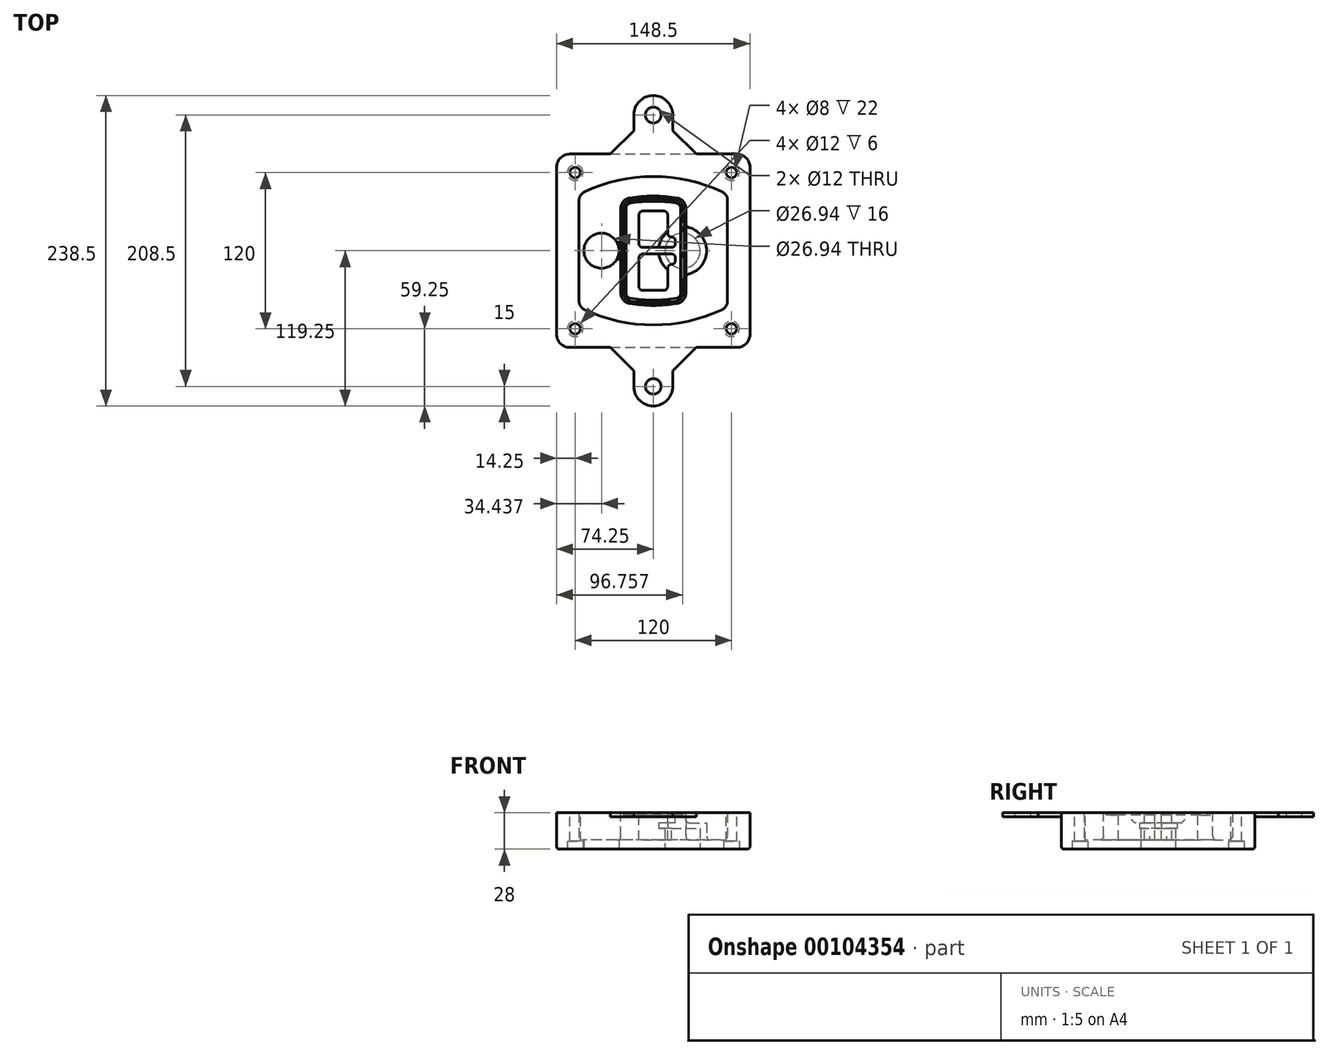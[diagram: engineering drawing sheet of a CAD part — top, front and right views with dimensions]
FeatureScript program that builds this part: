
annotation { "Feature Type Name" : "Feature", "Feature Type Description" : "" }
export const myFeature = defineFeature(function(context is Context, id is Id, definition is map)
    precondition{}
    {
        {
            var Q0;
            Q0=qCreatedBy(makeId("Top.planeOp"),FACE);
            var sketch = newSketch(context, id + "F0", { "sketchPlane" : qUnion([Q0])});
            skPoint(sketch, "E0.rect.middle", {"position": v(0, 0) * mm});
            skLineSegment(sketch, "E1.bottom", {"start": v(-64.25, -74.25) * mm, "end": v(64.25, -74.25) * mm});
            skLineSegment(sketch, "E1.top", {"start": v(-64.25, 74.25) * mm, "end": v(64.25, 74.25) * mm});
            skLineSegment(sketch, "E1.left", {"start": v(-74.25, -64.25) * mm, "end": v(-74.25, 64.25) * mm});
            skLineSegment(sketch, "E1.right", {"start": v(74.25, -64.25) * mm, "end": v(74.25, 64.25) * mm});
            skLineSegment(sketch, "E2", {"start": v(-74.25, 74.25) * mm, "end": v(74.25, -74.25) * mm, "construction": true});
            skLineSegment(sketch, "E3", {"start": v(74.25, 74.25) * mm, "end": v(-74.25, -74.25) * mm, "construction": true});
            skCircle(sketch, "E4", {"center": v(-60, 60) * mm, "radius": 4 * mm});
            skCircle(sketch, "E5", {"center": v(60, 60) * mm, "radius": 4 * mm});
            skCircle(sketch, "E6", {"center": v(60, -60) * mm, "radius": 4 * mm});
            skCircle(sketch, "E7", {"center": v(-60, -60) * mm, "radius": 4 * mm});
            skLineSegment(sketch, "E8", {"start": v(-60, 60) * mm, "end": v(60, 60) * mm, "construction": true});
            skLineSegment(sketch, "E9", {"start": v(60, 60) * mm, "end": v(60, -60) * mm, "construction": true});
            skLineSegment(sketch, "E10", {"start": v(60, -60) * mm, "end": v(-60, -60) * mm, "construction": true});
            skLineSegment(sketch, "E11", {"start": v(-60, -60) * mm, "end": v(-60, 60) * mm, "construction": true});
            skLineSegment(sketch, "E12", {"start": v(-60, 38.83) * mm, "end": v(-60, -38.83) * mm});
            skLineSegment(sketch, "E13", {"start": v(60, 38.83) * mm, "end": v(60, -38.83) * mm});
            skArc(sketch, "E14", {"start": v(54.26, 47.88) * mm, "mid": v(0, 60) * mm, "end": v(-54.26, 47.88) * mm});
            skArc(sketch, "E15", {"start": v(-54.26, -47.88) * mm, "mid": v(0, -60) * mm, "end": v(54.26, -47.88) * mm});
            skLineSegment(sketch, "E16", {"start": v(-60, 0) * mm, "end": v(60, 0) * mm, "construction": true});
            skPoint(sketch, "E17.visualSharp", {"position": v(-60, -45) * mm});
            skArc(sketch, "E17.filletArc", {"start": v(-60, -38.83) * mm, "mid": v(-58.44, -44.2) * mm, "end": v(-54.26, -47.88) * mm});
            skPoint(sketch, "E18.visualSharp", {"position": v(-60, 45) * mm});
            skArc(sketch, "E18.filletArc", {"start": v(-54.26, 47.88) * mm, "mid": v(-58.44, 44.2) * mm, "end": v(-60, 38.83) * mm});
            skPoint(sketch, "E19.visualSharp", {"position": v(60, 45) * mm});
            skArc(sketch, "E19.filletArc", {"start": v(60, 38.83) * mm, "mid": v(58.44, 44.2) * mm, "end": v(54.26, 47.88) * mm});
            skPoint(sketch, "E20.visualSharp", {"position": v(60, -45) * mm});
            skArc(sketch, "E20.filletArc", {"start": v(54.26, -47.88) * mm, "mid": v(58.44, -44.2) * mm, "end": v(60, -38.83) * mm});
            skPoint(sketch, "E21.visualSharp", {"position": v(-74.25, 74.25) * mm});
            skArc(sketch, "E21.filletArc", {"start": v(-64.25, 74.25) * mm, "mid": v(-71.32, 71.32) * mm, "end": v(-74.25, 64.25) * mm});
            skPoint(sketch, "E22.visualSharp", {"position": v(74.25, 74.25) * mm});
            skArc(sketch, "E22.filletArc", {"start": v(74.25, 64.25) * mm, "mid": v(71.32, 71.32) * mm, "end": v(64.25, 74.25) * mm});
            skPoint(sketch, "E23.visualSharp", {"position": v(74.25, -74.25) * mm});
            skArc(sketch, "E23.filletArc", {"start": v(64.25, -74.25) * mm, "mid": v(71.32, -71.32) * mm, "end": v(74.25, -64.25) * mm});
            skPoint(sketch, "E24.visualSharp", {"position": v(-74.25, -74.25) * mm});
            skArc(sketch, "E24.filletArc", {"start": v(-74.25, -64.25) * mm, "mid": v(-71.32, -71.32) * mm, "end": v(-64.25, -74.25) * mm});
            skArc(sketch, "E25.0", {"start": v(57, 38.83) * mm, "mid": v(55.9, 42.58) * mm, "end": v(52.98, 45.17) * mm});
            skLineSegment(sketch, "E25.1", {"start": v(57, 38.83) * mm, "end": v(57, -38.83) * mm});
            skArc(sketch, "E25.2", {"start": v(52.98, -45.17) * mm, "mid": v(55.9, -42.58) * mm, "end": v(57, -38.83) * mm});
            skArc(sketch, "E25.3", {"start": v(-52.98, -45.17) * mm, "mid": v(0, -57) * mm, "end": v(52.98, -45.17) * mm});
            skArc(sketch, "E25.4", {"start": v(-57, -38.83) * mm, "mid": v(-55.9, -42.58) * mm, "end": v(-52.98, -45.17) * mm});
            skArc(sketch, "E25.5", {"start": v(52.98, 45.17) * mm, "mid": v(0, 57) * mm, "end": v(-52.98, 45.17) * mm});
            skLineSegment(sketch, "E25.6", {"start": v(-57, 38.83) * mm, "end": v(-57, -38.83) * mm});
            skArc(sketch, "E25.7", {"start": v(-52.98, 45.17) * mm, "mid": v(-55.9, 42.58) * mm, "end": v(-57, 38.83) * mm});
            skArc(sketch, "E26.0", {"start": v(-55.96, 51.5) * mm, "mid": v(-61.82, 46.33) * mm, "end": v(-64, 38.83) * mm});
            skArc(sketch, "E26.1", {"start": v(55.96, 51.5) * mm, "mid": v(0, 64) * mm, "end": v(-55.96, 51.5) * mm});
            skArc(sketch, "E26.2", {"start": v(64, 38.83) * mm, "mid": v(61.82, 46.33) * mm, "end": v(55.96, 51.5) * mm});
            skLineSegment(sketch, "E26.3", {"start": v(64, 38.83) * mm, "end": v(64, -38.83) * mm});
            skArc(sketch, "E26.4", {"start": v(55.96, -51.5) * mm, "mid": v(61.82, -46.33) * mm, "end": v(64, -38.83) * mm});
            skLineSegment(sketch, "E26.5", {"start": v(-64, 38.83) * mm, "end": v(-64, -38.83) * mm});
            skArc(sketch, "E26.6", {"start": v(-55.96, -51.5) * mm, "mid": v(0, -64) * mm, "end": v(55.96, -51.5) * mm});
            skArc(sketch, "E26.7", {"start": v(-64, -38.83) * mm, "mid": v(-61.82, -46.33) * mm, "end": v(-55.96, -51.5) * mm});
            skSolve(sketch);
        }
        {
            var Q0;
            Q0=makeQuery(id+"F0.imprint","IMPRINT",FACE,{"disambiguationData":[TD([[makeQuery(id+"F0.imprint","IMPRINT",EDGE,{"derivedFrom":sQuery(id+"F0.wireOp",EDGE,"E1.bottom")}),1.0]])]});
            var Q1;
            Q1=makeQuery(id+"F0.imprint","IMPRINT",FACE,{"disambiguationData":[TD([[makeQuery(id+"F0.imprint","IMPRINT",EDGE,{"derivedFrom":sQuery(id+"F0.wireOp",EDGE,"E12")}),1.0]])]});
            var Q2;
            Q2=makeQuery(id+"F0.imprint","IMPRINT",FACE,{"disambiguationData":[TD([[makeQuery(id+"F0.imprint","IMPRINT",EDGE,{"derivedFrom":sQuery(id+"F0.wireOp",EDGE,"E25.0")}),1.0]])]});
            var Q3;
            Q3=makeQuery(id+"F0.imprint","IMPRINT",FACE,{"disambiguationData":[TD([[makeQuery(id+"F0.imprint","IMPRINT",EDGE,{"derivedFrom":sQuery(id+"F0.wireOp",EDGE,"E12")}),-1.0]])]});
            extrude(context, id + "F1", {"entities" : qUnion([Q0, Q1, Q2, Q3]), "oppositeDirection" : true, "depth" : 25 * mm});
        }
        {
            var Q0;
            Q0=makeQuery(id+"F0.imprint","IMPRINT",FACE,{"disambiguationData":[TD([[makeQuery(id+"F0.imprint","IMPRINT",EDGE,{"derivedFrom":sQuery(id+"F0.wireOp",EDGE,"E12")}),1.0]])]});
            extrude(context, id + "F2", {"entities" : qUnion([Q0]), "operationType" : NewBodyOperationType.ADD, "depth" : 3 * mm});
        }
        {
            var Q0;
            Q0=makeQuery(id+"F0.imprint","IMPRINT",FACE,{"disambiguationData":[TD([[makeQuery(id+"F0.imprint","IMPRINT",EDGE,{"derivedFrom":sQuery(id+"F0.wireOp",EDGE,"E25.0")}),1.0]])]});
            extrude(context, id + "F3", {"entities" : qUnion([Q0]), "operationType" : NewBodyOperationType.REMOVE, "oppositeDirection" : true, "depth" : 18 * mm});
        }
        {
            var Q0;
            Q0=makeQuery(id+"F2.opExtrude","CAP_FACE",FACE,{"disambiguationData":[OSD([sQuery(id+"F0.wireOp",EDGE,"E12"),sQuery(id+"F0.wireOp",EDGE,"E13"),sQuery(id+"F0.wireOp",EDGE,"E14"),sQuery(id+"F0.wireOp",EDGE,"E15"),sQuery(id+"F0.wireOp",EDGE,"E17.filletArc"),sQuery(id+"F0.wireOp",EDGE,"E18.filletArc"),sQuery(id+"F0.wireOp",EDGE,"E19.filletArc"),sQuery(id+"F0.wireOp",EDGE,"E20.filletArc"),sQuery(id+"F0.wireOp",EDGE,"E25.0"),sQuery(id+"F0.wireOp",EDGE,"E25.1"),sQuery(id+"F0.wireOp",EDGE,"E25.2"),sQuery(id+"F0.wireOp",EDGE,"E25.3"),sQuery(id+"F0.wireOp",EDGE,"E25.4"),sQuery(id+"F0.wireOp",EDGE,"E25.5"),sQuery(id+"F0.wireOp",EDGE,"E25.6"),sQuery(id+"F0.wireOp",EDGE,"E25.7")])],"isStart":false});
            var sketch = newSketch(context, id + "F4", { "sketchPlane" : qUnion([Q0])});
            skArc(sketch, "E27.0", {"start": v(-18.34, -40.45) * mm, "mid": v(0, -42) * mm, "end": v(18.34, -40.45) * mm});
            skArc(sketch, "E28.0", {"start": v(18.34, 40.45) * mm, "mid": v(0, 42) * mm, "end": v(-18.34, 40.45) * mm});
            skLineSegment(sketch, "E29", {"start": v(-25, 32.57) * mm, "end": v(-25, -32.57) * mm});
            skLineSegment(sketch, "E30", {"start": v(25, 32.57) * mm, "end": v(25, -32.57) * mm});
            skLineSegment(sketch, "E31", {"start": v(-25, 39.1) * mm, "end": v(25, 39.1) * mm, "construction": true});
            skLineSegment(sketch, "E32", {"start": v(-25, -39.1) * mm, "end": v(25, -39.1) * mm, "construction": true});
            skPoint(sketch, "E33.visualSharp", {"position": v(-25, 39.1) * mm});
            skArc(sketch, "E33.filletArc", {"start": v(-18.34, 40.45) * mm, "mid": v(-23.11, 37.73) * mm, "end": v(-25, 32.57) * mm});
            skPoint(sketch, "E34.visualSharp", {"position": v(25, 39.1) * mm});
            skArc(sketch, "E34.filletArc", {"start": v(25, 32.57) * mm, "mid": v(23.11, 37.73) * mm, "end": v(18.34, 40.45) * mm});
            skPoint(sketch, "E35.visualSharp", {"position": v(25, -39.1) * mm});
            skArc(sketch, "E35.filletArc", {"start": v(18.34, -40.45) * mm, "mid": v(23.11, -37.73) * mm, "end": v(25, -32.57) * mm});
            skPoint(sketch, "E36.visualSharp", {"position": v(-25, -39.1) * mm});
            skArc(sketch, "E36.filletArc", {"start": v(-25, -32.57) * mm, "mid": v(-23.11, -37.73) * mm, "end": v(-18.34, -40.45) * mm});
            skArc(sketch, "E37.0", {"start": v(52.98, 45.17) * mm, "mid": v(0, 57) * mm, "end": v(-52.98, 45.17) * mm});
            skArc(sketch, "E37.1", {"start": v(-52.98, 45.17) * mm, "mid": v(-55.9, 42.58) * mm, "end": v(-57, 38.83) * mm});
            skLineSegment(sketch, "E37.2", {"start": v(-57, 38.83) * mm, "end": v(-57, -38.83) * mm});
            skArc(sketch, "E37.3", {"start": v(-57, -38.83) * mm, "mid": v(-55.9, -42.58) * mm, "end": v(-52.98, -45.17) * mm});
            skArc(sketch, "E37.4", {"start": v(-52.98, -45.17) * mm, "mid": v(0, -57) * mm, "end": v(52.98, -45.17) * mm});
            skArc(sketch, "E37.5", {"start": v(52.98, -45.17) * mm, "mid": v(55.9, -42.58) * mm, "end": v(57, -38.83) * mm});
            skLineSegment(sketch, "E37.6", {"start": v(57, 38.83) * mm, "end": v(57, -38.83) * mm});
            skArc(sketch, "E37.7", {"start": v(57, 38.83) * mm, "mid": v(55.9, 42.58) * mm, "end": v(52.98, 45.17) * mm});
            skLineSegment(sketch, "E38.0", {"start": v(23, 32.57) * mm, "end": v(23, -32.57) * mm});
            skArc(sketch, "E38.1", {"start": v(18, -38.48) * mm, "mid": v(21.58, -36.44) * mm, "end": v(23, -32.57) * mm});
            skArc(sketch, "E38.2", {"start": v(-18, -38.48) * mm, "mid": v(0, -40) * mm, "end": v(18, -38.48) * mm});
            skArc(sketch, "E38.3", {"start": v(-23, -32.57) * mm, "mid": v(-21.58, -36.44) * mm, "end": v(-18, -38.48) * mm});
            skLineSegment(sketch, "E38.4", {"start": v(-23, 32.57) * mm, "end": v(-23, -32.57) * mm});
            skArc(sketch, "E38.5", {"start": v(23, 32.57) * mm, "mid": v(21.58, 36.44) * mm, "end": v(18, 38.48) * mm});
            skArc(sketch, "E38.6", {"start": v(-18, 38.48) * mm, "mid": v(-21.58, 36.44) * mm, "end": v(-23, 32.57) * mm});
            skArc(sketch, "E38.7", {"start": v(18, 38.48) * mm, "mid": v(0, 40) * mm, "end": v(-18, 38.48) * mm});
            skArc(sketch, "E39.0", {"start": v(21, 32.57) * mm, "mid": v(20.06, 35.15) * mm, "end": v(17.67, 36.5) * mm});
            skLineSegment(sketch, "E39.1", {"start": v(21, 32.57) * mm, "end": v(21, -32.57) * mm});
            skArc(sketch, "E39.2", {"start": v(17.67, -36.5) * mm, "mid": v(20.06, -35.15) * mm, "end": v(21, -32.57) * mm});
            skArc(sketch, "E39.3", {"start": v(-17.67, -36.5) * mm, "mid": v(0, -38) * mm, "end": v(17.67, -36.5) * mm});
            skArc(sketch, "E39.4", {"start": v(-21, -32.57) * mm, "mid": v(-20.06, -35.15) * mm, "end": v(-17.67, -36.5) * mm});
            skArc(sketch, "E39.5", {"start": v(17.67, 36.5) * mm, "mid": v(0, 38) * mm, "end": v(-17.67, 36.5) * mm});
            skLineSegment(sketch, "E39.6", {"start": v(-21, 32.57) * mm, "end": v(-21, -32.57) * mm});
            skArc(sketch, "E39.7", {"start": v(-17.67, 36.5) * mm, "mid": v(-20.06, 35.15) * mm, "end": v(-21, 32.57) * mm});
            skLineSegment(sketch, "E40", {"start": v(-25, 0) * mm, "end": v(25, 0) * mm, "construction": true});
            skLineSegment(sketch, "E41", {"start": v(-11, 5.5) * mm, "end": v(-11, 27.5) * mm});
            skLineSegment(sketch, "E42", {"start": v(-8, 30.5) * mm, "end": v(8, 30.5) * mm});
            skLineSegment(sketch, "E43", {"start": v(11, 27.5) * mm, "end": v(11, 13.5) * mm});
            skLineSegment(sketch, "E44", {"start": v(14, 10.5) * mm, "end": v(14, 10.5) * mm});
            skLineSegment(sketch, "E45", {"start": v(17, 7.5) * mm, "end": v(17, 5.5) * mm});
            skLineSegment(sketch, "E46", {"start": v(14, 2.5) * mm, "end": v(-8, 2.5) * mm});
            skPoint(sketch, "E47.visualSharp", {"position": v(-11, 30.5) * mm});
            skArc(sketch, "E47.filletArc", {"start": v(-8, 30.5) * mm, "mid": v(-10.12, 29.62) * mm, "end": v(-11, 27.5) * mm});
            skPoint(sketch, "E48.visualSharp", {"position": v(11, 30.5) * mm});
            skArc(sketch, "E48.filletArc", {"start": v(11, 27.5) * mm, "mid": v(10.12, 29.62) * mm, "end": v(8, 30.5) * mm});
            skPoint(sketch, "E49.visualSharp", {"position": v(11, 10.5) * mm});
            skArc(sketch, "E49.filletArc", {"start": v(11, 13.5) * mm, "mid": v(11.88, 11.38) * mm, "end": v(14, 10.5) * mm});
            skPoint(sketch, "E50.visualSharp", {"position": v(17, 10.5) * mm});
            skArc(sketch, "E50.filletArc", {"start": v(17, 7.5) * mm, "mid": v(16.12, 9.62) * mm, "end": v(14, 10.5) * mm});
            skPoint(sketch, "E51.visualSharp", {"position": v(17, 2.5) * mm});
            skArc(sketch, "E51.filletArc", {"start": v(14, 2.5) * mm, "mid": v(16.12, 3.38) * mm, "end": v(17, 5.5) * mm});
            skPoint(sketch, "E52.visualSharp", {"position": v(-11, 2.5) * mm});
            skArc(sketch, "E52.filletArc", {"start": v(-11, 5.5) * mm, "mid": v(-10.12, 3.38) * mm, "end": v(-8, 2.5) * mm});
            skLineSegment(sketch, "E53.0.MirrorCS", {"start": v(14, -2.5) * mm, "end": v(-8, -2.5) * mm});
            skArc(sketch, "E54.0.MirrorCS", {"start": v(-11, -5.5) * mm, "mid": v(-10.12, -3.38) * mm, "end": v(-8, -2.5) * mm});
            skLineSegment(sketch, "E55.0.MirrorCS", {"start": v(-11, -5.5) * mm, "end": v(-11, -27.5) * mm});
            skArc(sketch, "E56.0.MirrorCS", {"start": v(-8, -30.5) * mm, "mid": v(-10.12, -29.62) * mm, "end": v(-11, -27.5) * mm});
            skLineSegment(sketch, "E57.0.MirrorCS", {"start": v(-8, -30.5) * mm, "end": v(8, -30.5) * mm});
            skArc(sketch, "E58.0.MirrorCS", {"start": v(11, -27.5) * mm, "mid": v(10.12, -29.62) * mm, "end": v(8, -30.5) * mm});
            skLineSegment(sketch, "E59.0.MirrorCS", {"start": v(11, -27.5) * mm, "end": v(11, -13.5) * mm});
            skArc(sketch, "E60.0.MirrorCS", {"start": v(11, -13.5) * mm, "mid": v(11.88, -11.38) * mm, "end": v(14, -10.5) * mm});
            skArc(sketch, "E61.0.MirrorCS", {"start": v(17, -7.5) * mm, "mid": v(16.12, -9.62) * mm, "end": v(14, -10.5) * mm});
            skLineSegment(sketch, "E62.0.MirrorCS", {"start": v(17, -7.5) * mm, "end": v(17, -5.5) * mm});
            skArc(sketch, "E63.0.MirrorCS", {"start": v(14, -2.5) * mm, "mid": v(16.12, -3.38) * mm, "end": v(17, -5.5) * mm});
            skSolve(sketch);
        }
        {
            var Q0;
            Q0=makeQuery(id+"F4.imprint","IMPRINT",FACE,{"disambiguationData":[TD([[makeQuery(id+"F4.imprint","IMPRINT",EDGE,{"derivedFrom":sQuery(id+"F4.wireOp",EDGE,"E27.0")}),1.0]])]});
            var Q1;
            Q1=makeQuery(id+"F4.imprint","IMPRINT",FACE,{"disambiguationData":[TD([[makeQuery(id+"F4.imprint","IMPRINT",EDGE,{"derivedFrom":sQuery(id+"F4.wireOp",EDGE,"E38.0")}),-1.0]])]});
            var Q2;
            Q2=makeQuery(id+"F4.imprint","IMPRINT",FACE,{"disambiguationData":[TD([[makeQuery(id+"F4.imprint","IMPRINT",EDGE,{"derivedFrom":sQuery(id+"F4.wireOp",EDGE,"E39.0")}),1.0]])]});
            extrude(context, id + "F5", {"entities" : qUnion([Q0, Q1, Q2]), "operationType" : NewBodyOperationType.ADD, "endBound" : BoundingType.UP_TO_NEXT, "oppositeDirection" : true, "depth" : 25 * mm});
        }
        {
            var Q0;
            Q0=makeQuery(id+"F4.imprint","IMPRINT",FACE,{"disambiguationData":[TD([[makeQuery(id+"F4.imprint","IMPRINT",EDGE,{"derivedFrom":sQuery(id+"F4.wireOp",EDGE,"E38.0")}),-1.0]])]});
            extrude(context, id + "F6", {"entities" : qUnion([Q0]), "operationType" : NewBodyOperationType.REMOVE, "oppositeDirection" : true, "depth" : 2 * mm});
        }
        {
            var Q0;
            Q0=makeQuery(id+"F1.opExtrude","CAP_FACE",FACE,{"disambiguationData":[OSD([sQuery(id+"F0.wireOp",EDGE,"E1.bottom"),sQuery(id+"F0.wireOp",EDGE,"E1.top"),sQuery(id+"F0.wireOp",EDGE,"E1.left"),sQuery(id+"F0.wireOp",EDGE,"E1.right"),sQuery(id+"F0.wireOp",EDGE,"E4"),sQuery(id+"F0.wireOp",EDGE,"E5"),sQuery(id+"F0.wireOp",EDGE,"E6"),sQuery(id+"F0.wireOp",EDGE,"E7"),sQuery(id+"F0.wireOp",EDGE,"E21.filletArc"),sQuery(id+"F0.wireOp",EDGE,"E22.filletArc"),sQuery(id+"F0.wireOp",EDGE,"E23.filletArc"),sQuery(id+"F0.wireOp",EDGE,"E24.filletArc")])],"isStart":false});
            var sketch = newSketch(context, id + "F7", { "sketchPlane" : qUnion([Q0])});
            skCircle(sketch, "E64", {"center": v(22.5, 0) * mm, "radius": 13.47 * mm});
            skCircle(sketch, "E65", {"center": v(-39.81, 0) * mm, "radius": 13.47 * mm});
            skLineSegment(sketch, "E66", {"start": v(74.25, 0) * mm, "end": v(-74.25, 0) * mm});
            skCircle(sketch, "E67", {"center": v(22.5, 0) * mm, "radius": 18.47 * mm});
            skCircle(sketch, "E68", {"center": v(60, -60) * mm, "radius": 6 * mm});
            skCircle(sketch, "E69", {"center": v(-60, -60) * mm, "radius": 6 * mm});
            skCircle(sketch, "E70", {"center": v(-60, 60) * mm, "radius": 6 * mm});
            skCircle(sketch, "E71", {"center": v(60, 60) * mm, "radius": 6 * mm});
            skSolve(sketch);
        }
        {
            var Q0;
            {var subQ1=sQuery(id+"F7.wireOp",EDGE,"E66");var subQ4=sQuery(id+"F7.wireOp",EDGE,"E64");var subQ6=makeQuery(id+"F7.imprint","INTERSECT",VERTEX,{"disambiguationData":[OD(0.0)],"derivedFrom":[subQ4,subQ1]});Q0=makeQuery(id+"F7.imprint","IMPRINT",FACE,{"disambiguationData":[TD([[makeQuery(id+"F7.imprint","IMPRINT",EDGE,{"disambiguationData":[TD([[subQ6,-1.0]])],"derivedFrom":subQ4}),-1.0]])]});}
            var Q1;
            {var subQ0=sQuery(id+"F7.wireOp",EDGE,"E66");var subQ1=sQuery(id+"F7.wireOp",EDGE,"E64");var subQ3=makeQuery(id+"F7.imprint","INTERSECT",VERTEX,{"disambiguationData":[OD(0.0)],"derivedFrom":[subQ1,subQ0]});Q1=makeQuery(id+"F7.imprint","IMPRINT",FACE,{"disambiguationData":[TD([[makeQuery(id+"F7.imprint","IMPRINT",EDGE,{"disambiguationData":[TD([[subQ3,-1.0]])],"derivedFrom":subQ1}),1.0]])]});}
            var Q2;
            {var subQ0=sQuery(id+"F7.wireOp",EDGE,"E66");var subQ1=sQuery(id+"F7.wireOp",EDGE,"E64");var subQ3=makeQuery(id+"F7.imprint","INTERSECT",VERTEX,{"disambiguationData":[OD(0.0)],"derivedFrom":[subQ1,subQ0]});Q2=makeQuery(id+"F7.imprint","IMPRINT",FACE,{"disambiguationData":[TD([[makeQuery(id+"F7.imprint","IMPRINT",EDGE,{"disambiguationData":[TD([[subQ3,1.0]])],"derivedFrom":subQ1}),1.0]])]});}
            var Q3;
            {var subQ1=sQuery(id+"F7.wireOp",EDGE,"E66");var subQ4=sQuery(id+"F7.wireOp",EDGE,"E64");var subQ6=makeQuery(id+"F7.imprint","INTERSECT",VERTEX,{"disambiguationData":[OD(0.0)],"derivedFrom":[subQ4,subQ1]});Q3=makeQuery(id+"F7.imprint","IMPRINT",FACE,{"disambiguationData":[TD([[makeQuery(id+"F7.imprint","IMPRINT",EDGE,{"disambiguationData":[TD([[subQ6,1.0]])],"derivedFrom":subQ4}),-1.0]])]});}
            extrude(context, id + "F8", {"entities" : qUnion([Q0, Q1, Q2, Q3]), "operationType" : NewBodyOperationType.ADD, "oppositeDirection" : true, "depth" : 20 * mm});
        }
        {
            var Q0;
            {var subQ0=sQuery(id+"F7.wireOp",EDGE,"E66");var subQ1=sQuery(id+"F7.wireOp",EDGE,"E64");var subQ3=makeQuery(id+"F7.imprint","INTERSECT",VERTEX,{"disambiguationData":[OD(0.0)],"derivedFrom":[subQ1,subQ0]});Q0=makeQuery(id+"F7.imprint","IMPRINT",FACE,{"disambiguationData":[TD([[makeQuery(id+"F7.imprint","IMPRINT",EDGE,{"disambiguationData":[TD([[subQ3,-1.0]])],"derivedFrom":subQ1}),1.0]])]});}
            var Q1;
            {var subQ0=sQuery(id+"F7.wireOp",EDGE,"E66");var subQ1=sQuery(id+"F7.wireOp",EDGE,"E64");var subQ3=makeQuery(id+"F7.imprint","INTERSECT",VERTEX,{"disambiguationData":[OD(0.0)],"derivedFrom":[subQ1,subQ0]});Q1=makeQuery(id+"F7.imprint","IMPRINT",FACE,{"disambiguationData":[TD([[makeQuery(id+"F7.imprint","IMPRINT",EDGE,{"disambiguationData":[TD([[subQ3,1.0]])],"derivedFrom":subQ1}),1.0]])]});}
            extrude(context, id + "F9", {"entities" : qUnion([Q0, Q1]), "operationType" : NewBodyOperationType.REMOVE, "oppositeDirection" : true, "depth" : 16 * mm});
        }
        {
            var Q0;
            {var subQ0=sQuery(id+"F7.wireOp",EDGE,"E66");var subQ1=sQuery(id+"F7.wireOp",EDGE,"E65");var subQ3=makeQuery(id+"F7.imprint","INTERSECT",VERTEX,{"disambiguationData":[OD(0.0)],"derivedFrom":[subQ1,subQ0]});Q0=makeQuery(id+"F7.imprint","IMPRINT",FACE,{"disambiguationData":[TD([[makeQuery(id+"F7.imprint","IMPRINT",EDGE,{"disambiguationData":[TD([[subQ3,-1.0]])],"derivedFrom":subQ1}),1.0]])]});}
            var Q1;
            {var subQ0=sQuery(id+"F7.wireOp",EDGE,"E66");var subQ1=sQuery(id+"F7.wireOp",EDGE,"E65");var subQ3=makeQuery(id+"F7.imprint","INTERSECT",VERTEX,{"disambiguationData":[OD(0.0)],"derivedFrom":[subQ1,subQ0]});Q1=makeQuery(id+"F7.imprint","IMPRINT",FACE,{"disambiguationData":[TD([[makeQuery(id+"F7.imprint","IMPRINT",EDGE,{"disambiguationData":[TD([[subQ3,1.0]])],"derivedFrom":subQ1}),1.0]])]});}
            extrude(context, id + "F10", {"entities" : qUnion([Q0, Q1]), "operationType" : NewBodyOperationType.REMOVE, "oppositeDirection" : true, "depth" : 25 * mm});
        }
        {
            var Q0;
            Q0=makeQuery(id+"F7.imprint","IMPRINT",FACE,{"disambiguationData":[TD([[makeQuery(id+"F7.imprint","IMPRINT",EDGE,{"derivedFrom":sQuery(id+"F7.wireOp",EDGE,"E68")}),1.0]])]});
            var Q1;
            Q1=makeQuery(id+"F7.imprint","IMPRINT",FACE,{"disambiguationData":[TD([[makeQuery(id+"F7.imprint","IMPRINT",EDGE,{"derivedFrom":makeQuery(id+"F1.opExtrude","CAP_EDGE",EDGE,{"disambiguationData":[OSD([sQuery(id+"F0.wireOp",EDGE,"E5")])],"isStart":false})}),-1.0]])]});
            var Q2;
            Q2=makeQuery(id+"F7.imprint","IMPRINT",FACE,{"disambiguationData":[TD([[makeQuery(id+"F7.imprint","IMPRINT",EDGE,{"derivedFrom":sQuery(id+"F7.wireOp",EDGE,"E69")}),1.0]])]});
            var Q3;
            Q3=makeQuery(id+"F7.imprint","IMPRINT",FACE,{"disambiguationData":[TD([[makeQuery(id+"F7.imprint","IMPRINT",EDGE,{"derivedFrom":makeQuery(id+"F1.opExtrude","CAP_EDGE",EDGE,{"disambiguationData":[OSD([sQuery(id+"F0.wireOp",EDGE,"E4")])],"isStart":false})}),-1.0]])]});
            var Q4;
            Q4=makeQuery(id+"F7.imprint","IMPRINT",FACE,{"disambiguationData":[TD([[makeQuery(id+"F7.imprint","IMPRINT",EDGE,{"derivedFrom":sQuery(id+"F7.wireOp",EDGE,"E70")}),1.0]])]});
            var Q5;
            Q5=makeQuery(id+"F7.imprint","IMPRINT",FACE,{"disambiguationData":[TD([[makeQuery(id+"F7.imprint","IMPRINT",EDGE,{"derivedFrom":makeQuery(id+"F1.opExtrude","CAP_EDGE",EDGE,{"disambiguationData":[OSD([sQuery(id+"F0.wireOp",EDGE,"E7")])],"isStart":false})}),-1.0]])]});
            var Q6;
            Q6=makeQuery(id+"F7.imprint","IMPRINT",FACE,{"disambiguationData":[TD([[makeQuery(id+"F7.imprint","IMPRINT",EDGE,{"derivedFrom":sQuery(id+"F7.wireOp",EDGE,"E71")}),1.0]])]});
            var Q7;
            Q7=makeQuery(id+"F7.imprint","IMPRINT",FACE,{"disambiguationData":[TD([[makeQuery(id+"F7.imprint","IMPRINT",EDGE,{"derivedFrom":makeQuery(id+"F1.opExtrude","CAP_EDGE",EDGE,{"disambiguationData":[OSD([sQuery(id+"F0.wireOp",EDGE,"E6")])],"isStart":false})}),-1.0]])]});
            extrude(context, id + "F11", {"entities" : qUnion([Q0, Q1, Q2, Q3, Q4, Q5, Q6, Q7]), "operationType" : NewBodyOperationType.REMOVE, "oppositeDirection" : true, "depth" : 6 * mm});
        }
        {
            var Q0;
            Q0=makeQuery(id+"F9.boolean.opBoolean","COPY",FACE,{"derivedFrom":makeQuery(id+"F9.opExtrude","CAP_FACE",FACE,{"disambiguationData":[OSD([sQuery(id+"F7.wireOp",EDGE,"E64")])],"isStart":false})});
            var sketch = newSketch(context, id + "F12", { "sketchPlane" : qUnion([Q0])});
            skArc(sketch, "E72.0", {"start": v(11, 14.45) * mm, "mid": v(6.45, 9.13) * mm, "end": v(4.2, 2.5) * mm});
            skArc(sketch, "E72.1", {"start": v(4.2, -2.5) * mm, "mid": v(6.45, -9.13) * mm, "end": v(11, -14.45) * mm});
            skLineSegment(sketch, "E73", {"start": v(4.2, -2.5) * mm, "end": v(14, -2.5) * mm});
            skLineSegment(sketch, "E74.0", {"start": v(14, 2.5) * mm, "end": v(4.2, 2.5) * mm});
            skArc(sketch, "E74.1", {"start": v(14, 2.5) * mm, "mid": v(16.12, 3.38) * mm, "end": v(17, 5.5) * mm});
            skLineSegment(sketch, "E74.2", {"start": v(17, 7.5) * mm, "end": v(17, 5.5) * mm});
            skArc(sketch, "E74.3", {"start": v(17, 7.5) * mm, "mid": v(16.12, 9.62) * mm, "end": v(14, 10.5) * mm});
            skArc(sketch, "E74.4", {"start": v(11, 13.5) * mm, "mid": v(11.88, 11.38) * mm, "end": v(14, 10.5) * mm});
            skLineSegment(sketch, "E74.5", {"start": v(11, 14.45) * mm, "end": v(11, 13.5) * mm});
            skLineSegment(sketch, "E74.7", {"start": v(14, -2.5) * mm, "end": v(4.2, -2.5) * mm});
            skArc(sketch, "E74.8", {"start": v(14, -2.5) * mm, "mid": v(16.12, -3.38) * mm, "end": v(17, -5.5) * mm});
            skLineSegment(sketch, "E74.9", {"start": v(17, -7.5) * mm, "end": v(17, -5.5) * mm});
            skArc(sketch, "E74.10", {"start": v(17, -7.5) * mm, "mid": v(16.12, -9.62) * mm, "end": v(14, -10.5) * mm});
            skArc(sketch, "E74.11", {"start": v(11, -13.5) * mm, "mid": v(11.88, -11.38) * mm, "end": v(14, -10.5) * mm});
            skLineSegment(sketch, "E74.12", {"start": v(11, -14.45) * mm, "end": v(11, -13.5) * mm});
            skPoint(sketch, "E75.orphan", {"position": v(11, -27.5) * mm});
            skPoint(sketch, "E76.orphan", {"position": v(-8, -2.5) * mm});
            skPoint(sketch, "E77.orphan", {"position": v(-8, 2.5) * mm});
            skPoint(sketch, "E78.orphan", {"position": v(11, 27.5) * mm});
            skSolve(sketch);
        }
        {
            var Q0;
            {var subQ7=sQuery(id+"F12.wireOp",EDGE,"E72.0");var subQ14=sQuery(id+"F12.wireOp",EDGE,"E72.1");var subQ16=sQuery(id+"F12.wireOp",EDGE,"E74.1");var subQ18=sQuery(id+"F12.wireOp",EDGE,"E74.8");Q0=qUnion([makeQuery(id+"F12.imprint","IMPRINT",FACE,{"disambiguationData":[TD([[makeQuery(id+"F12.imprint","IMPRINT",EDGE,{"derivedFrom":subQ7}),1.0]])]}),makeQuery(id+"F12.imprint","IMPRINT",FACE,{"disambiguationData":[TD([[makeQuery(id+"F12.imprint","IMPRINT",EDGE,{"derivedFrom":subQ14}),1.0]])]}),makeQuery(id+"F12.imprint","IMPRINT",FACE,{"disambiguationData":[TD([[makeQuery(id+"F12.imprint","IMPRINT",EDGE,{"derivedFrom":subQ16}),1.0]])]}),makeQuery(id+"F12.imprint","IMPRINT",FACE,{"disambiguationData":[TD([[makeQuery(id+"F12.imprint","IMPRINT",EDGE,{"derivedFrom":subQ18}),-1.0]])]})]);}
            var Q1;
            Q1=makeQuery(id+"F5.boolean.opBoolean","SPLIT",FACE,{"disambiguationData":[TD([makeQuery(id+"F5.opExtrude","SWEPT_FACE",FACE,{"disambiguationData":[OSD([sQuery(id+"F4.wireOp",EDGE,"E41")])]})])],"derivedFrom":makeQuery(id+"F3.boolean.opBoolean","COPY",FACE,{"derivedFrom":makeQuery(id+"F3.opExtrude","CAP_FACE",FACE,{"disambiguationData":[OSD([sQuery(id+"F0.wireOp",EDGE,"E25.0"),sQuery(id+"F0.wireOp",EDGE,"E25.1"),sQuery(id+"F0.wireOp",EDGE,"E25.2"),sQuery(id+"F0.wireOp",EDGE,"E25.3"),sQuery(id+"F0.wireOp",EDGE,"E25.4"),sQuery(id+"F0.wireOp",EDGE,"E25.5"),sQuery(id+"F0.wireOp",EDGE,"E25.6"),sQuery(id+"F0.wireOp",EDGE,"E25.7")])],"isStart":false})})});
            extrude(context, id + "F13", {"entities" : qUnion([Q0]), "operationType" : NewBodyOperationType.REMOVE, "endBound" : BoundingType.UP_TO_SURFACE, "endBoundEntityFace" : qUnion([Q1]), "depth" : 25 * mm});
        }
        {
            var Q0;
            Q0=makeQuery(id+"F3.boolean.opBoolean","COPY",EDGE,{"derivedFrom":makeQuery(id+"F3.opExtrude","CAP_EDGE",EDGE,{"disambiguationData":[OSD([sQuery(id+"F0.wireOp",EDGE,"E25.6")])],"isStart":false})});
            var Q1;
            Q1=makeQuery(id+"F8.boolean.opBoolean","INTERSECT",EDGE,{"derivedFrom":[makeQuery(id+"F5.opExtrude","SWEPT_FACE",FACE,{"disambiguationData":[OSD([sQuery(id+"F4.wireOp",EDGE,"E30")])]}),makeQuery(id+"F8.opExtrude","CAP_FACE",FACE,{"disambiguationData":[OSD([sQuery(id+"F7.wireOp",EDGE,"E67")])],"isStart":false})]});
            var Q2;
            Q2=makeQuery(id+"F8.boolean.opBoolean","INTERSECT",EDGE,{"disambiguationData":[OD(1.0)],"derivedFrom":[makeQuery(id+"F5.opExtrude","SWEPT_FACE",FACE,{"disambiguationData":[OSD([sQuery(id+"F4.wireOp",EDGE,"E30")])]}),makeQuery(id+"F8.opExtrude","SWEPT_FACE",FACE,{"disambiguationData":[OSD([sQuery(id+"F7.wireOp",EDGE,"E67")])]})]});
            var Q3;
            {var subQ0=sQuery(id+"F4.wireOp",EDGE,"E30");Q3=makeQuery(id+"F8.boolean.opBoolean","SPLIT",EDGE,{"disambiguationData":[TD([makeQuery(id+"F5.opExtrude","SWEPT_FACE",FACE,{"disambiguationData":[OSD([sQuery(id+"F4.wireOp",EDGE,"E35.filletArc")])]})])],"derivedFrom":makeQuery(id+"F5.opExtrude","CAP_EDGE",EDGE,{"disambiguationData":[OSD([subQ0])],"isStart":false})});}
            var Q4;
            {var subQ0=sQuery(id+"F0.wireOp",EDGE,"E25.7");var subQ1=sQuery(id+"F0.wireOp",EDGE,"E25.1");var subQ2=sQuery(id+"F0.wireOp",EDGE,"E25.6");var subQ3=sQuery(id+"F0.wireOp",EDGE,"E25.5");var subQ4=sQuery(id+"F0.wireOp",EDGE,"E25.4");var subQ5=sQuery(id+"F0.wireOp",EDGE,"E25.0");var subQ6=sQuery(id+"F0.wireOp",EDGE,"E25.2");var subQ7=sQuery(id+"F0.wireOp",EDGE,"E25.3");Q4=makeQuery(id+"F8.boolean.opBoolean","INTERSECT",EDGE,{"derivedFrom":[makeQuery(id+"F5.boolean.opBoolean","SPLIT",FACE,{"disambiguationData":[TD([makeQuery(id+"F2.opExtrude","SWEPT_FACE",FACE,{"disambiguationData":[OSD([subQ5])]})])],"derivedFrom":makeQuery(id+"F3.boolean.opBoolean","COPY",FACE,{"derivedFrom":makeQuery(id+"F3.opExtrude","CAP_FACE",FACE,{"disambiguationData":[OSD([subQ5,subQ1,subQ6,subQ7,subQ4,subQ3,subQ2,subQ0])],"isStart":false})})}),makeQuery(id+"F8.opExtrude","SWEPT_FACE",FACE,{"disambiguationData":[OSD([sQuery(id+"F7.wireOp",EDGE,"E67")])]})]});}
            var Q5;
            Q5=makeQuery(id+"F8.boolean.opBoolean","INTERSECT",EDGE,{"disambiguationData":[OD(0.0)],"derivedFrom":[makeQuery(id+"F5.opExtrude","SWEPT_FACE",FACE,{"disambiguationData":[OSD([sQuery(id+"F4.wireOp",EDGE,"E30")])]}),makeQuery(id+"F8.opExtrude","SWEPT_FACE",FACE,{"disambiguationData":[OSD([sQuery(id+"F7.wireOp",EDGE,"E67")])]})]});
            fillet(context, id + "F14", {"entities" : qUnion([Q0, Q1, Q2, Q3, Q4, Q5]), "radius" : 3 * mm, "tangentPropagation" : true, "allowEdgeOverflow" : false});
        }
        {
            var Q0;
            Q0=makeQuery(id+"F1.opExtrude","CAP_EDGE",EDGE,{"disambiguationData":[OSD([sQuery(id+"F0.wireOp",EDGE,"E1.bottom")])],"isStart":false});
            fillet(context, id + "F15", {"entities" : qUnion([Q0]), "radius" : 2 * mm, "tangentPropagation" : true, "allowEdgeOverflow" : false});
        }
        {
            var Q0;
            {var subQ0=sQuery(id+"F0.wireOp",EDGE,"E22.filletArc");var subQ1=sQuery(id+"F0.wireOp",EDGE,"E7");var subQ2=sQuery(id+"F0.wireOp",EDGE,"E6");var subQ3=sQuery(id+"F0.wireOp",EDGE,"E5");var subQ4=sQuery(id+"F0.wireOp",EDGE,"E4");var subQ5=sQuery(id+"F0.wireOp",EDGE,"E1.bottom");var subQ6=sQuery(id+"F0.wireOp",EDGE,"E21.filletArc");var subQ7=sQuery(id+"F0.wireOp",EDGE,"E1.top");var subQ8=sQuery(id+"F0.wireOp",EDGE,"E1.left");var subQ9=sQuery(id+"F0.wireOp",EDGE,"E1.right");var subQ10=sQuery(id+"F0.wireOp",EDGE,"E23.filletArc");var subQ11=sQuery(id+"F0.wireOp",EDGE,"E24.filletArc");Q0=makeQuery(id+"F2.boolean.opBoolean","SPLIT",FACE,{"disambiguationData":[TD([makeQuery(id+"F1.opExtrude","SWEPT_FACE",FACE,{"disambiguationData":[OSD([subQ5])]})])],"derivedFrom":makeQuery(id+"F1.opExtrude","CAP_FACE",FACE,{"disambiguationData":[OSD([subQ5,subQ7,subQ8,subQ9,subQ4,subQ3,subQ2,subQ1,subQ6,subQ0,subQ10,subQ11])],"isStart":true})});}
            var sketch = newSketch(context, id + "F16", { "sketchPlane" : qUnion([Q0])});
            skLineSegment(sketch, "E79", {"start": v(0, 74.25) * mm, "end": v(0, 104.25) * mm, "construction": true});
            skPoint(sketch, "E79.endSnap0", {"position": v(0, 74.25) * mm});
            skCircle(sketch, "E80", {"center": v(0, 104.25) * mm, "radius": 6 * mm});
            skLineSegment(sketch, "E81", {"start": v(-33, 74.25) * mm, "end": v(-15, 92.25) * mm});
            skLineSegment(sketch, "E82", {"start": v(-15, 92.25) * mm, "end": v(-15, 104.25) * mm});
            skLineSegment(sketch, "E83", {"start": v(15, 104.25) * mm, "end": v(15, 92.25) * mm});
            skLineSegment(sketch, "E84", {"start": v(15, 92.25) * mm, "end": v(33, 74.25) * mm});
            skArc(sketch, "E85", {"start": v(15, 104.25) * mm, "mid": v(0, 119.25) * mm, "end": v(-15, 104.25) * mm});
            skLineSegment(sketch, "E86", {"start": v(-74.25, 0) * mm, "end": v(74.25, 0) * mm, "construction": true});
            skLineSegment(sketch, "E87.MirrorCS", {"start": v(-33, -74.25) * mm, "end": v(-15, -92.25) * mm});
            skLineSegment(sketch, "E88.MirrorCS", {"start": v(-15, -92.25) * mm, "end": v(-15, -104.25) * mm});
            skArc(sketch, "E89.MirrorCS", {"start": v(15, -104.25) * mm, "mid": v(0, -119.25) * mm, "end": v(-15, -104.25) * mm});
            skLineSegment(sketch, "E90.MirrorCS", {"start": v(15, -104.25) * mm, "end": v(15, -92.25) * mm});
            skLineSegment(sketch, "E91.MirrorCS", {"start": v(15, -92.25) * mm, "end": v(33, -74.25) * mm});
            skCircle(sketch, "E92.MirrorC", {"center": v(0, -104.25) * mm, "radius": 6 * mm});
            skSolve(sketch);
        }
        {
            var Q0;
            {var subQ0=sQuery(id+"F16.wireOp",EDGE,"E87.MirrorCS");Q0=makeQuery(id+"F16.imprint","IMPRINT",FACE,{"disambiguationData":[TD([[makeQuery(id+"F16.imprint","IMPRINT",EDGE,{"derivedFrom":subQ0}),1.0]])]});}
            var Q1;
            Q1=makeQuery(id+"F16.imprint","IMPRINT",FACE,{"disambiguationData":[TD([[makeQuery(id+"F16.imprint","IMPRINT",EDGE,{"derivedFrom":sQuery(id+"F16.wireOp",EDGE,"E80")}),-1.0]])]});
            var Q2;
            Q2=makeQuery(id+"F16.imprint","IMPRINT",FACE,{"disambiguationData":[TD([[makeQuery(id+"F16.imprint","IMPRINT",EDGE,{"derivedFrom":makeQuery(id+"F1.opExtrude","CAP_EDGE",EDGE,{"disambiguationData":[OSD([sQuery(id+"F0.wireOp",EDGE,"E1.left")])],"isStart":true})}),-1.0]])]});
            var Q3;
            Q3=makeQuery(id+"F2.opExtrude","CAP_FACE",FACE,{"disambiguationData":[OSD([sQuery(id+"F0.wireOp",EDGE,"E12"),sQuery(id+"F0.wireOp",EDGE,"E13"),sQuery(id+"F0.wireOp",EDGE,"E14"),sQuery(id+"F0.wireOp",EDGE,"E15"),sQuery(id+"F0.wireOp",EDGE,"E17.filletArc"),sQuery(id+"F0.wireOp",EDGE,"E18.filletArc"),sQuery(id+"F0.wireOp",EDGE,"E19.filletArc"),sQuery(id+"F0.wireOp",EDGE,"E20.filletArc"),sQuery(id+"F0.wireOp",EDGE,"E25.0"),sQuery(id+"F0.wireOp",EDGE,"E25.1"),sQuery(id+"F0.wireOp",EDGE,"E25.2"),sQuery(id+"F0.wireOp",EDGE,"E25.3"),sQuery(id+"F0.wireOp",EDGE,"E25.4"),sQuery(id+"F0.wireOp",EDGE,"E25.5"),sQuery(id+"F0.wireOp",EDGE,"E25.6"),sQuery(id+"F0.wireOp",EDGE,"E25.7")])],"isStart":false});
            extrude(context, id + "F17", {"entities" : qUnion([Q0, Q1, Q2]), "operationType" : NewBodyOperationType.ADD, "endBound" : BoundingType.UP_TO_SURFACE, "endBoundEntityFace" : qUnion([Q3]), "depth" : 25 * mm});
        }
    });
